# Revit family: Breezy
name_source: partatom
category: Оборудование
units: mm (PartAtom-declared; Revit-internal decimal feet)

## family parameters
Всегда вертикально = Да
Классификация = Нет
На основе рабочей плоскости = Нет
Общий = Нет
При загрузке вырезать с полостями = Нет
Размер круглого соединителя = Использовать диаметр
Тип детали = Нормальный
Точка принадлежности помещению = Нет

## types (2) — shared parameters
00_20_Manufacturer = Вентс
00_20_Name = Провітрювач
Casing Material = Металл, окрашенный, синий, матовый RAL 5007
Grid Material = Cover Grid Cross
Load Classification = HVAC
Maintenance zone material = <По категории>
Number of Fase = 1
Power = 100 Вт
Voltage = 230 В
l = 450 мм
zero-valued in all types: Отметка по умолчанию

## per-type parameters (varying)
| type | -R1 | -r | D1 | Dn | Dy | Maximum Air Flow | R1 | Вага | Рівень звукового тиску на відстані 3 м |
| Breezy 160 | -95 мм | -55 мм | 190 мм | 165 мм | 160 мм | 57.0 м³/ч | 95 мм | 6.50 кг | 35 дБА |
| Breezy 200 | -115 мм | -75 мм | 230 мм | 205 мм | 200 мм | 95.0 м³/ч | 115 мм | 7.00 кг | 34 дБА |

note: column(s) folded — value = type name in every type: 00_20_Type
